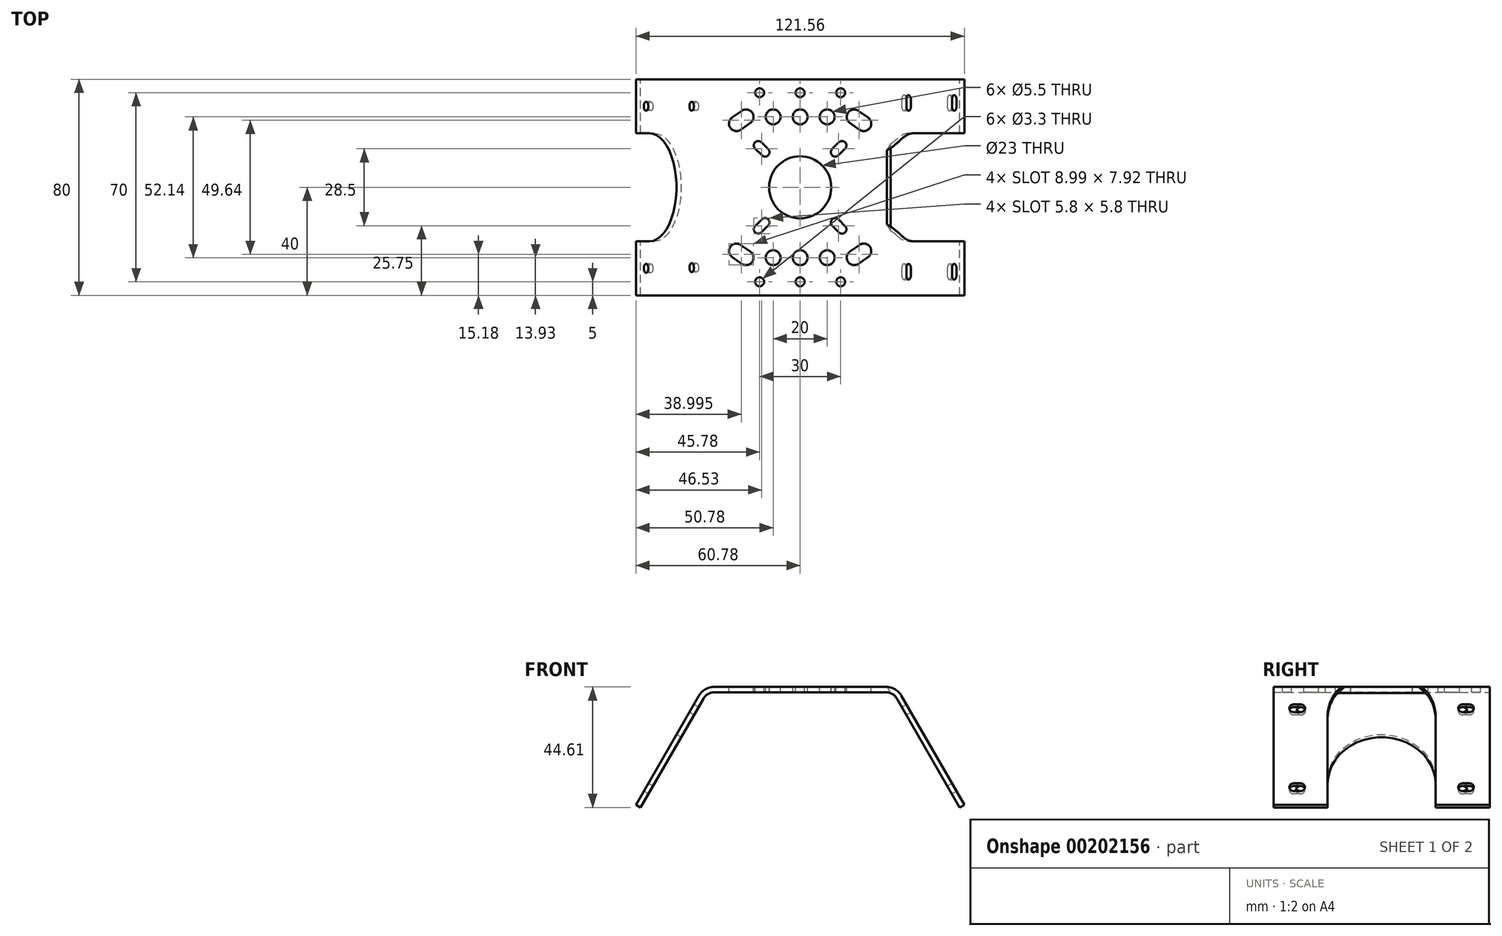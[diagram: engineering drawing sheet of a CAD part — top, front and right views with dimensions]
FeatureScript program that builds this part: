
annotation { "Feature Type Name" : "Feature", "Feature Type Description" : "" }
export const myFeature = defineFeature(function(context is Context, id is Id, definition is map)
    precondition{}
    {
        {
            var Q0;
            Q0=qCreatedBy(makeId("Front.planeOp"),FACE);
            var sketch = newSketch(context, id + "F0", { "sketchPlane" : qUnion([Q0])});
            skLineSegment(sketch, "E0", {"start": v(-31.85, 0) * mm, "end": v(31.85, 0) * mm});
            skLineSegment(sketch, "E1", {"start": v(-35.75, -2.25) * mm, "end": v(-59.05, -42.6) * mm});
            skLineSegment(sketch, "E2", {"start": v(35.75, -2.25) * mm, "end": v(59.05, -42.6) * mm});
            skPoint(sketch, "E3.visualSharp", {"position": v(-34.45, 0) * mm});
            skArc(sketch, "E3.filletArc", {"start": v(-31.85, 0) * mm, "mid": v(-34.1, -0.6) * mm, "end": v(-35.75, -2.25) * mm});
            skPoint(sketch, "E4.visualSharp", {"position": v(34.45, 0) * mm});
            skArc(sketch, "E4.filletArc", {"start": v(35.75, -2.25) * mm, "mid": v(34.1, -0.6) * mm, "end": v(31.85, 0) * mm});
            skLineSegment(sketch, "E5.0", {"start": v(37.48, -1.25) * mm, "end": v(60.78, -41.6) * mm});
            skLineSegment(sketch, "E5.1", {"start": v(-37.48, -1.25) * mm, "end": v(-60.78, -41.6) * mm});
            skArc(sketch, "E5.2", {"start": v(-31.85, 2) * mm, "mid": v(-35.1, 1.13) * mm, "end": v(-37.48, -1.25) * mm});
            skLineSegment(sketch, "E5.3", {"start": v(-31.85, 2) * mm, "end": v(31.85, 2) * mm});
            skArc(sketch, "E5.4", {"start": v(37.48, -1.25) * mm, "mid": v(35.1, 1.13) * mm, "end": v(31.85, 2) * mm});
            skLineSegment(sketch, "E6", {"start": v(-60.78, -41.6) * mm, "end": v(-59.05, -42.6) * mm});
            skLineSegment(sketch, "E7", {"start": v(60.78, -41.6) * mm, "end": v(59.05, -42.6) * mm});
            skSolve(sketch);
        }
        {
            var Q0;
            Q0=qSketchRegion(id+"F0",true);
            var Q1;
            Q1=qConstructionFilter(qBodyType(qCreatedBy(id+"F0",EDGE),BodyType.WIRE),ConstructionObject.NO);
            extrude(context, id + "F1", {"entities" : qUnion([Q0]), "surfaceEntities" : qUnion([Q1]), "depth" : 80 * mm});
        }
        {
            var Q0;
            Q0=makeQuery(id+"F1.opExtrude","SWEPT_FACE",FACE,{"disambiguationData":[OSD([sQuery(id+"F0.wireOp",EDGE,"E5.0")])]});
            var sketch = newSketch(context, id + "F2", { "sketchPlane" : qUnion([Q0])});
            skArc(sketch, "E8", {"start": v(-20, -28.88) * mm, "mid": v(-40, -8.88) * mm, "end": v(-60, -28.88) * mm});
            skLineSegment(sketch, "E9", {"start": v(-20, -28.88) * mm, "end": v(-20, -66.42) * mm});
            skLineSegment(sketch, "E10", {"start": v(-60, -28.88) * mm, "end": v(-60, -66.42) * mm});
            skLineSegment(sketch, "E11", {"start": v(-20, -66.42) * mm, "end": v(0, -66.42) * mm});
            skLineSegment(sketch, "E12", {"start": v(0, -66.42) * mm, "end": v(0, -19.82) * mm});
            skLineSegment(sketch, "E13", {"start": v(-20, -66.42) * mm, "end": v(-60, -66.42) * mm});
            skArc(sketch, "E14", {"start": v(-70, -60.57) * mm, "mid": v(-68.35, -58.92) * mm, "end": v(-70, -57.27) * mm});
            skArc(sketch, "E15", {"start": v(-72.5, -57.27) * mm, "mid": v(-74.15, -58.92) * mm, "end": v(-72.5, -60.57) * mm});
            skArc(sketch, "E16", {"start": v(-72.5, -23.52) * mm, "mid": v(-74.15, -25.17) * mm, "end": v(-72.5, -26.82) * mm});
            skArc(sketch, "E17", {"start": v(-70, -26.82) * mm, "mid": v(-68.35, -25.17) * mm, "end": v(-70, -23.52) * mm});
            skArc(sketch, "E18", {"start": v(-7.5, -26.82) * mm, "mid": v(-5.85, -25.17) * mm, "end": v(-7.5, -23.52) * mm});
            skArc(sketch, "E19", {"start": v(-10, -23.52) * mm, "mid": v(-11.65, -25.17) * mm, "end": v(-10, -26.82) * mm});
            skArc(sketch, "E20", {"start": v(-7.5, -60.57) * mm, "mid": v(-5.85, -58.92) * mm, "end": v(-7.5, -57.27) * mm});
            skArc(sketch, "E21", {"start": v(-10, -57.27) * mm, "mid": v(-11.65, -58.92) * mm, "end": v(-10, -60.57) * mm});
            skLineSegment(sketch, "E22", {"start": v(-7.5, -23.52) * mm, "end": v(-10, -23.52) * mm});
            skLineSegment(sketch, "E23", {"start": v(-7.5, -26.82) * mm, "end": v(-10, -26.82) * mm});
            skLineSegment(sketch, "E24", {"start": v(-7.5, -57.27) * mm, "end": v(-10, -57.27) * mm});
            skLineSegment(sketch, "E25", {"start": v(-7.5, -60.57) * mm, "end": v(-10, -60.57) * mm});
            skLineSegment(sketch, "E26", {"start": v(-70, -23.52) * mm, "end": v(-72.5, -23.52) * mm});
            skLineSegment(sketch, "E27", {"start": v(-70, -26.82) * mm, "end": v(-72.5, -26.82) * mm});
            skLineSegment(sketch, "E28", {"start": v(-70, -57.27) * mm, "end": v(-72.5, -57.27) * mm});
            skLineSegment(sketch, "E29", {"start": v(-70, -60.57) * mm, "end": v(-72.5, -60.57) * mm});
            skSolve(sketch);
        }
        {
            var Q0;
            Q0=qSketchRegion(id+"F2",true);
            extrude(context, id + "F3", {"entities" : qUnion([Q0]), "operationType" : NewBodyOperationType.REMOVE, "oppositeDirection" : true, "depth" : 3 * mm});
        }
        {
            var Q0;
            Q0=makeQuery(id+"F1.opExtrude","SWEPT_FACE",FACE,{"disambiguationData":[OSD([sQuery(id+"F0.wireOp",EDGE,"E5.1")])]});
            var sketch = newSketch(context, id + "F4", { "sketchPlane" : qUnion([Q0])});
            skCircle(sketch, "E30", {"center": v(40, -56.42) * mm, "radius": 20 * mm});
            skCircle(sketch, "E31", {"center": v(70, -58.92) * mm, "radius": 1.65 * mm});
            skCircle(sketch, "E32", {"center": v(69.75, -25.17) * mm, "radius": 1.65 * mm});
            skCircle(sketch, "E33", {"center": v(10, -58.92) * mm, "radius": 1.65 * mm});
            skCircle(sketch, "E34", {"center": v(10, -25.17) * mm, "radius": 1.65 * mm});
            skLineSegment(sketch, "E35.bottom", {"start": v(20, -56.42) * mm, "end": v(60, -56.42) * mm});
            skLineSegment(sketch, "E35.top", {"start": v(20, -66.42) * mm, "end": v(60, -66.42) * mm});
            skLineSegment(sketch, "E35.left", {"start": v(20, -56.42) * mm, "end": v(20, -66.42) * mm});
            skLineSegment(sketch, "E35.right", {"start": v(60, -56.42) * mm, "end": v(60, -66.42) * mm});
            skSolve(sketch);
        }
        {
            var Q0;
            Q0=qSketchRegion(id+"F4",true);
            extrude(context, id + "F5", {"entities" : qUnion([Q0]), "operationType" : NewBodyOperationType.REMOVE, "oppositeDirection" : true, "depth" : 3 * mm});
        }
        {
            var Q0;
            Q0=makeQuery(id+"F1.opExtrude","SWEPT_FACE",FACE,{"disambiguationData":[OSD([sQuery(id+"F0.wireOp",EDGE,"E5.3")])]});
            var sketch = newSketch(context, id + "F6", { "sketchPlane" : qUnion([Q0])});
            skCircle(sketch, "E36", {"center": v(0, -40) * mm, "radius": 11.5 * mm});
            skCircle(sketch, "E37", {"center": v(-15, -5) * mm, "radius": 1.65 * mm});
            skCircle(sketch, "E38", {"center": v(0, -5) * mm, "radius": 1.65 * mm});
            skCircle(sketch, "E39", {"center": v(15, -5) * mm, "radius": 1.65 * mm});
            skCircle(sketch, "E40", {"center": v(-10, -13.93) * mm, "radius": 2.75 * mm});
            skCircle(sketch, "E41", {"center": v(0, -13.93) * mm, "radius": 2.75 * mm});
            skCircle(sketch, "E42", {"center": v(10, -13.93) * mm, "radius": 2.75 * mm});
            skCircle(sketch, "E43", {"center": v(-10, -66.07) * mm, "radius": 2.75 * mm});
            skCircle(sketch, "E44", {"center": v(0, -66.07) * mm, "radius": 2.75 * mm});
            skCircle(sketch, "E45", {"center": v(10, -66.07) * mm, "radius": 2.75 * mm});
            skCircle(sketch, "E46", {"center": v(0, -75) * mm, "radius": 1.65 * mm});
            skCircle(sketch, "E47", {"center": v(-15, -75) * mm, "radius": 1.65 * mm});
            skCircle(sketch, "E48", {"center": v(15, -75) * mm, "radius": 1.65 * mm});
            skLineSegment(sketch, "E49", {"start": v(-22, -61.32) * mm, "end": v(-18.42, -63.82) * mm});
            skLineSegment(sketch, "E50", {"start": v(-21.58, -68.32) * mm, "end": v(-25.15, -65.82) * mm});
            skLineSegment(sketch, "E51", {"start": v(-25.15, -14.18) * mm, "end": v(-21.58, -11.68) * mm});
            skLineSegment(sketch, "E52", {"start": v(-18.42, -16.18) * mm, "end": v(-22, -18.68) * mm});
            skLineSegment(sketch, "E53", {"start": v(21.58, -11.68) * mm, "end": v(25.15, -14.18) * mm});
            skLineSegment(sketch, "E54", {"start": v(18.42, -16.18) * mm, "end": v(22, -18.68) * mm});
            skLineSegment(sketch, "E55", {"start": v(18.42, -63.82) * mm, "end": v(22, -61.32) * mm});
            skLineSegment(sketch, "E56", {"start": v(25.15, -65.82) * mm, "end": v(21.58, -68.32) * mm});
            skArc(sketch, "E57", {"start": v(-14.33, -23.33) * mm, "mid": v(-16.67, -23.33) * mm, "end": v(-16.67, -25.67) * mm});
            skArc(sketch, "E58", {"start": v(-14.17, -28.17) * mm, "mid": v(-11.83, -28.17) * mm, "end": v(-11.83, -25.83) * mm});
            skArc(sketch, "E59", {"start": v(-11.83, -54.17) * mm, "mid": v(-11.83, -51.83) * mm, "end": v(-14.17, -51.83) * mm});
            skArc(sketch, "E60", {"start": v(-16.67, -54.33) * mm, "mid": v(-16.67, -56.67) * mm, "end": v(-14.33, -56.67) * mm});
            skArc(sketch, "E61", {"start": v(14.17, -51.83) * mm, "mid": v(11.83, -51.83) * mm, "end": v(11.83, -54.17) * mm});
            skArc(sketch, "E62", {"start": v(14.33, -56.67) * mm, "mid": v(16.67, -56.67) * mm, "end": v(16.67, -54.33) * mm});
            skArc(sketch, "E63", {"start": v(11.83, -25.83) * mm, "mid": v(11.83, -28.17) * mm, "end": v(14.17, -28.17) * mm});
            skArc(sketch, "E64", {"start": v(16.67, -25.67) * mm, "mid": v(16.67, -23.33) * mm, "end": v(14.33, -23.33) * mm});
            skLineSegment(sketch, "E65", {"start": v(-16.67, -25.67) * mm, "end": v(-14.17, -28.17) * mm});
            skLineSegment(sketch, "E66", {"start": v(-14.33, -23.33) * mm, "end": v(-11.83, -25.83) * mm});
            skLineSegment(sketch, "E67", {"start": v(-14.17, -51.83) * mm, "end": v(-16.67, -54.33) * mm});
            skLineSegment(sketch, "E68", {"start": v(-14.33, -56.67) * mm, "end": v(-11.83, -54.17) * mm});
            skLineSegment(sketch, "E69", {"start": v(11.83, -54.17) * mm, "end": v(14.33, -56.67) * mm});
            skLineSegment(sketch, "E70", {"start": v(16.67, -54.33) * mm, "end": v(14.17, -51.83) * mm});
            skLineSegment(sketch, "E71", {"start": v(11.83, -25.83) * mm, "end": v(14.33, -23.33) * mm});
            skLineSegment(sketch, "E72", {"start": v(14.17, -28.17) * mm, "end": v(16.67, -25.67) * mm});
            skArc(sketch, "E73", {"start": v(18.42, -63.82) * mm, "mid": v(17.75, -67.65) * mm, "end": v(21.58, -68.32) * mm});
            skArc(sketch, "E74", {"start": v(25.15, -65.82) * mm, "mid": v(25.82, -62) * mm, "end": v(22, -61.32) * mm});
            skArc(sketch, "E75", {"start": v(-22, -61.32) * mm, "mid": v(-25.82, -62) * mm, "end": v(-25.15, -65.82) * mm});
            skArc(sketch, "E76", {"start": v(-21.58, -68.32) * mm, "mid": v(-17.75, -67.65) * mm, "end": v(-18.42, -63.82) * mm});
            skArc(sketch, "E77", {"start": v(-18.42, -16.18) * mm, "mid": v(-17.75, -12.35) * mm, "end": v(-21.58, -11.68) * mm});
            skArc(sketch, "E78", {"start": v(-25.15, -14.18) * mm, "mid": v(-25.82, -18) * mm, "end": v(-22, -18.68) * mm});
            skArc(sketch, "E79", {"start": v(21.58, -11.68) * mm, "mid": v(17.75, -12.35) * mm, "end": v(18.42, -16.18) * mm});
            skArc(sketch, "E80", {"start": v(22, -18.68) * mm, "mid": v(25.82, -18) * mm, "end": v(25.15, -14.18) * mm});
            skSolve(sketch);
        }
        {
            var Q0;
            Q0=qSketchRegion(id+"F6",true);
            extrude(context, id + "F7", {"entities" : qUnion([Q0]), "operationType" : NewBodyOperationType.REMOVE, "oppositeDirection" : true, "depth" : 3 * mm});
        }
    });
